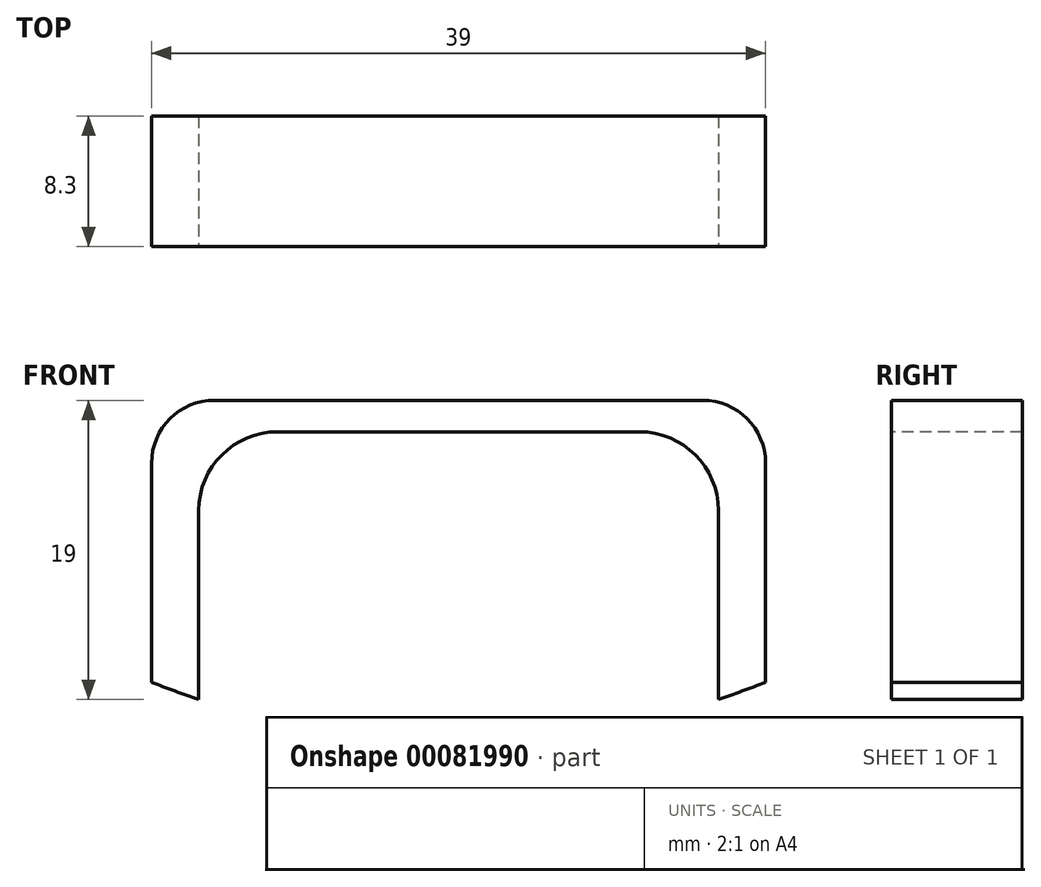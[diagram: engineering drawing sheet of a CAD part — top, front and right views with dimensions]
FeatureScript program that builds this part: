
annotation { "Feature Type Name" : "Feature", "Feature Type Description" : "" }
export const myFeature = defineFeature(function(context is Context, id is Id, definition is map)
    precondition{}
    {
        {
            var Q0;
            Q0=qCreatedBy(makeId("Front.planeOp"),FACE);
            var sketch = newSketch(context, id + "F0", { "sketchPlane" : qUnion([Q0])});
            skLineSegment(sketch, "E0.top", {"start": v(4, 0) * mm, "end": v(35, 0) * mm});
            skLineSegment(sketch, "E0.left", {"start": v(0, -17.9) * mm, "end": v(0, -4) * mm});
            skLineSegment(sketch, "E0.right", {"start": v(39, -17.9) * mm, "end": v(39, -4) * mm});
            skPoint(sketch, "E1.visualSharp", {"position": v(0, 0) * mm});
            skArc(sketch, "E1.filletArc", {"start": v(4, 0) * mm, "mid": v(1.17, -1.17) * mm, "end": v(0, -4) * mm});
            skArc(sketch, "E2.filletArc", {"start": v(39, -4) * mm, "mid": v(37.83, -1.17) * mm, "end": v(35, 0) * mm});
            skLineSegment(sketch, "E3.top", {"start": v(8, -2) * mm, "end": v(31, -2) * mm});
            skLineSegment(sketch, "E3.left", {"start": v(3, -19) * mm, "end": v(3, -7) * mm});
            skLineSegment(sketch, "E3.right", {"start": v(36, -19) * mm, "end": v(36, -7) * mm});
            skArc(sketch, "E4.filletArc", {"start": v(8, -2) * mm, "mid": v(4.46, -3.46) * mm, "end": v(3, -7) * mm});
            skArc(sketch, "E5.filletArc", {"start": v(36, -7) * mm, "mid": v(34.54, -3.46) * mm, "end": v(31, -2) * mm});
            skArc(sketch, "E6", {"start": v(0, -17.9) * mm, "mid": v(1.5, -18.48) * mm, "end": v(3, -19) * mm});
            skArc(sketch, "E7.trimOffspring", {"start": v(36, -19) * mm, "mid": v(37.5, -18.48) * mm, "end": v(39, -17.9) * mm});
            skSolve(sketch);
        }
        {
            var Q0;
            Q0=makeQuery(id+"F0.imprint","IMPRINT",FACE,{"disambiguationData":[TD([[makeQuery(id+"F0.imprint","IMPRINT",EDGE,{"derivedFrom":sQuery(id+"F0.wireOp",EDGE,"E0.top")}),-1.0]])]});
            extrude(context, id + "F1", {"entities" : qUnion([Q0]), "oppositeDirection" : true, "depth" : 8.3 * mm});
        }
    });
